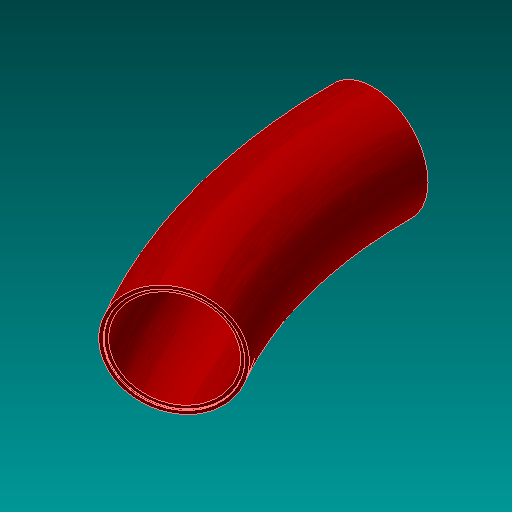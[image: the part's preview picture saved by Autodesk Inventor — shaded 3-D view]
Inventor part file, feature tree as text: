
AUTODESK INVENTOR PART (.ipt)
format: ipt  version: 2017.3 (Build 213257000, 257)  size: 232,960 bytes
history: native  units: in
note: dims shown in document units (in); Inventor stores cm internally (conversion verified against a paired STEP export)
features: extrude x4, sketch x4, revolve x2, fillet x1, chamfer x1
ambient origin geometry x8: Origin, YZ Plane, XZ Plane, XY Plane, X Axis, Y Axis, Z Axis, Center Point
bodies: Solid1 (feature_tree)
feature tree (12):
  revolve  "Revolution1"  [1 undecoded]
  extrude  "Extrusion9"  TaperAngle=30.0deg  [1 undecoded]
  sketch  "Sketch11"  dims[d34=30.5in d35=0.5in d36=0.0in]
  revolve  "Revolution3"  [1 undecoded]
  extrude  "Extrusion10"  Depth=0.0312in TaperAngle=0.0deg
  extrude  "Extrusion12"  Depth=0.0312in
  extrude  "Extrusion13"  Depth=0.0312in TaperAngle=45.0deg
  fillet  "Fillet3"  Radius=0.0034in
  chamfer  "Chamfer3"  Distance=0.25in
  sketch  "Sketch1"  dims[d0=28.5in d1=32.5in]
  sketch  "Sketch10"  dims[d2=160.0in d3=30.0deg]
  sketch  "Sketch12"  dims[d37=30.5in d39=0.25in d40=0.0in d44=0.0312in d45=0.0312in d46=0.125in d47=45.0deg d48=0.0034in d50=0.25in d51=0.0in d52=36.5in d53=0.25in d54=0.0in]
note: 3 required parameter values undecoded (feature->parameter linkage not recoverable at this tier; creation-order binding heuristic only, values carry confidence <= 0.55)